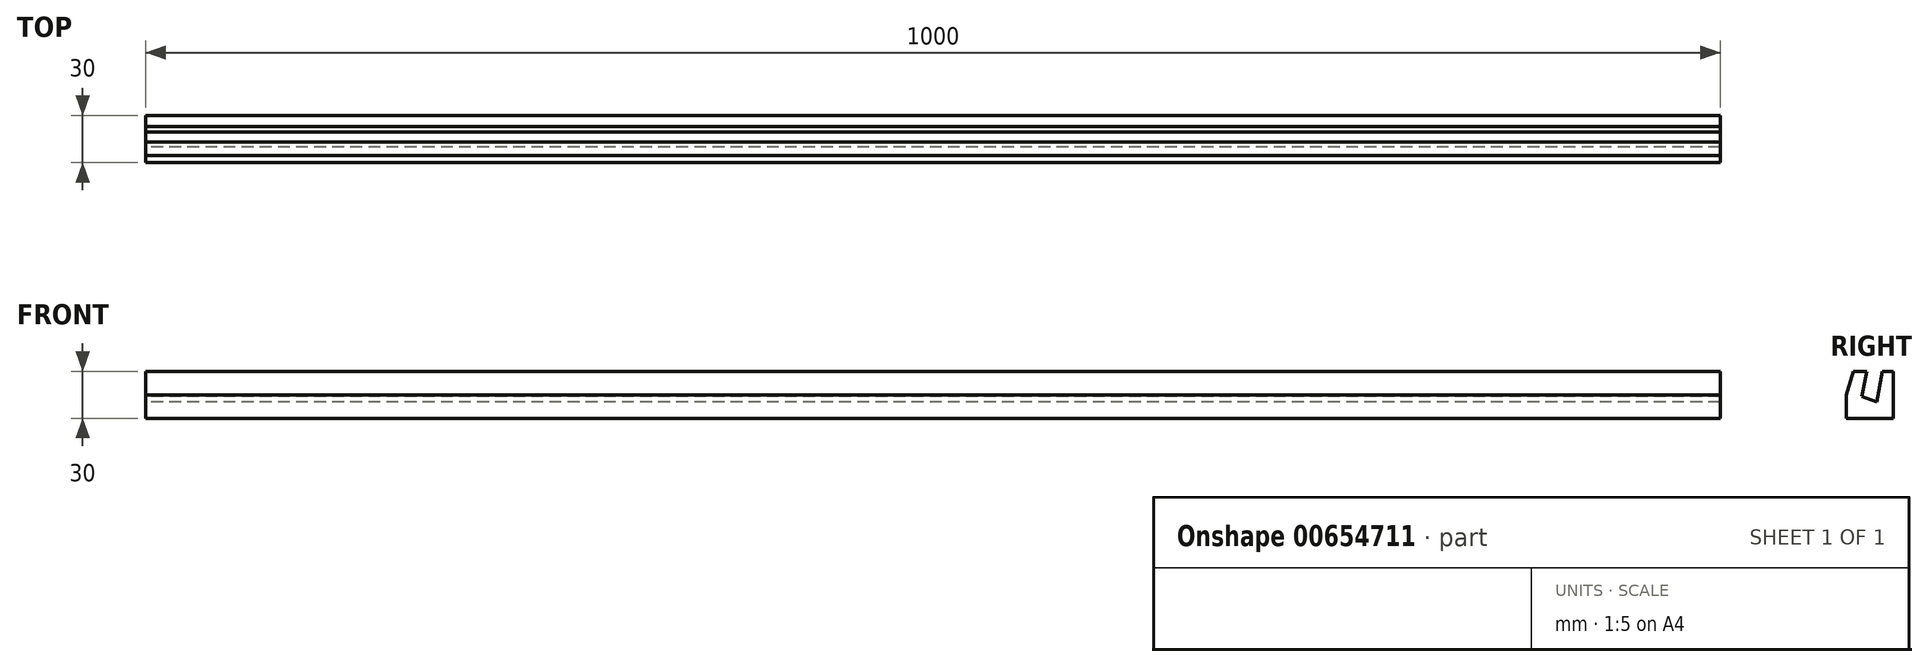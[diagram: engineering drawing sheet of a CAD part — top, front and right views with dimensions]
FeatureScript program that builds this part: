
annotation { "Feature Type Name" : "Feature", "Feature Type Description" : "" }
export const myFeature = defineFeature(function(context is Context, id is Id, definition is map)
    precondition{}
    {
        {
            var Q0;
            Q0=qCreatedBy(makeId("Front.planeOp"),FACE);
            var sketch = newSketch(context, id + "F0", { "sketchPlane" : qUnion([Q0])});
            skLineSegment(sketch, "E0.bottom", {"start": v(-1000, 39.8) * mm, "end": v(0, 39.8) * mm});
            skLineSegment(sketch, "E0.top", {"start": v(-1000, 9.8) * mm, "end": v(0, 9.8) * mm});
            skLineSegment(sketch, "E0.left", {"start": v(-1000, 39.8) * mm, "end": v(-1000, 9.8) * mm});
            skLineSegment(sketch, "E0.right", {"start": v(0, 39.8) * mm, "end": v(0, 9.8) * mm});
            skSolve(sketch);
        }
        {
            var Q0;
            Q0 = qSketchRegion(id + "F0", true);
            extrude(context, id + "F1", {"entities" : qUnion([Q0]), "depth" : 30 * mm, "offsetDistance" : 25 * mm});
        }
        {
            var Q0;
            Q0=makeQuery(id+"F1.opExtrude","SWEPT_FACE",FACE,{"disambiguationData":[OSD([sQuery(id+"F0.wireOp",EDGE,"E0.left")])]});
            var sketch = newSketch(context, id + "F2", { "sketchPlane" : qUnion([Q0])});
            skLineSegment(sketch, "E1", {"start": v(16.9, 39.8) * mm, "end": v(6.9, 39.8) * mm});
            skLineSegment(sketch, "E2", {"start": v(6.9, 39.8) * mm, "end": v(10.4, 20.2) * mm});
            skLineSegment(sketch, "E3", {"start": v(10.4, 20.2) * mm, "end": v(20.22, 23.72) * mm});
            skLineSegment(sketch, "E4", {"start": v(16.9, 39.8) * mm, "end": v(20.22, 23.72) * mm});
            skSolve(sketch);
        }
        {
            var Q0;
            Q0=makeQuery(id+"F2.imprint","IMPRINT",FACE,{"disambiguationData":[TD([[makeQuery(id+"F2.imprint","IMPRINT",EDGE,{"derivedFrom":sQuery(id+"F2.wireOp",EDGE,"E1")}),1.0]])]});
            extrude(context, id + "F3", {"entities" : qUnion([Q0]), "operationType" : NewBodyOperationType.REMOVE, "oppositeDirection" : true, "depth" : 2027 * mm, "offsetDistance" : 25 * mm});
        }
        {
            var Q0;
            Q0=makeQuery(id+"F1.opExtrude","SWEPT_FACE",FACE,{"disambiguationData":[OSD([sQuery(id+"F0.wireOp",EDGE,"E0.left")])]});
            var sketch = newSketch(context, id + "F4", { "sketchPlane" : qUnion([Q0])});
            skLineSegment(sketch, "E5", {"start": v(22.5, 49.8) * mm, "end": v(30, 24.8) * mm});
            skLineSegment(sketch, "E6", {"start": v(30, 24.8) * mm, "end": v(30, 39.8) * mm});
            skLineSegment(sketch, "E7", {"start": v(22.5, 49.8) * mm, "end": v(30, 39.8) * mm});
            skSolve(sketch);
        }
        {
            var Q0;
            Q0=makeQuery(id+"F4.imprint","IMPRINT",FACE,{"disambiguationData":[TD([[makeQuery(id+"F4.imprint","IMPRINT",EDGE,{"derivedFrom":sQuery(id+"F4.wireOp",EDGE,"E5")}),1.0]])]});
            extrude(context, id + "F5", {"entities" : qUnion([Q0]), "operationType" : NewBodyOperationType.REMOVE, "oppositeDirection" : true, "depth" : 2087 * mm, "offsetDistance" : 25 * mm});
        }
    });
